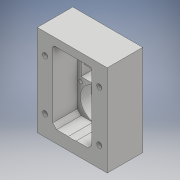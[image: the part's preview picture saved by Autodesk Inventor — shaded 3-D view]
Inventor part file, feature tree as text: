
AUTODESK INVENTOR PART (.ipt)
format: ipt  version: 2018 (Build 220112000, 112)  size: 443,904 bytes
history: native  units: mm
features: sketch x22, projected_geometry x19, extrude x18, hole x4, fillet x3, chamfer x1, mirror x1
ambient origin geometry x8: Origin, YZ Plane, XZ Plane, XY Plane, X Axis, Y Axis, Z Axis, Center Point
bodies: Solid1 (feature_tree)
feature tree (68):
  extrude  "Extrusion1"  Depth=45.0mm
  extrude  "Extrusion2"  Depth=1.95mm
  hole  "Hole1"  [1 undecoded]
  hole  "Hole2"  [1 undecoded]
  fillet  "Fillet1"  Radius=14.0mm
  extrude  "Extrusion3"  Depth=18.5mm
  extrude  "Extrusion4"  Depth=10.0mm
  extrude  "Extrusion5"  Depth=2.195mm
  extrude  "Extrusion6"  Depth=20.5mm
  hole  "Hole3"  [1 undecoded]
  extrude  "Extrusion7"  Depth=0.5mm
  extrude  "Extrusion8"  Depth=5.0mm TaperAngle=0.0deg
  extrude  "Extrusion9"  Depth=10.0mm
  extrude  "Extrusion10"  Depth=10.0mm
  extrude  "Extrusion11"  Depth=14.5mm
  extrude  "Extrusion12"  Depth=20.0mm
  extrude  "Extrusion13"  Depth=5.0mm
  extrude  "Extrusion14"  Depth=5.0mm
  extrude  "Extrusion15"  Depth=5.0mm
  extrude  "Extrusion16"  Depth=5.0mm
  extrude  "Extrusion17"  Depth=5.0mm
  chamfer  "Chamfer1"  Distance=1.0mm
  fillet  "Fillet7"  Radius=20.7mm
  fillet  "Fillet8"  Radius=32.0mm
  mirror  "Mirror1"
  extrude  "Extrusion18"  Depth=5.0mm TaperAngle=0.0deg
  hole  "Hole5"  [1 undecoded]
  sketch  "Sketch1"  dims[d0=24.5mm d1=45.0mm]
  sketch  "Sketch2"  dims[d2=1.95mm d3=0.0mm d4=2.25mm]
  projected_geometry  "Projected Loop1"
  sketch  "Sketch3"  dims[d5=20.0mm d6=2.25mm]
  projected_geometry  "Projected Loop2"
  sketch  "Sketch4"  dims[d7=5.25mm d8=5.25mm d9=14.0mm]
  projected_geometry  "Projected Loop3"
  sketch  "Sketch5"  dims[d10=5.25mm d11=18.5mm]
  projected_geometry  "Projected Loop4"
  sketch  "Sketch6"  dims[d12=10.0mm d13=0.0mm d14=20.5mm]
  projected_geometry  "Projected Loop5"
  sketch  "Sketch7"  dims[d15=2.0mm d16=2.195mm]
  projected_geometry  "Projected Loop6"
  sketch  "Sketch8"  dims[d17=2.0mm]
  projected_geometry  "Projected Loop7"
  sketch  "Sketch9"  dims[d18=2.4mm d19=6.0mm d20=4.4mm d21=2.0mm d22=90.0deg d23=8.0mm d24=20.594885mm d25=20.5mm]
  projected_geometry  "Projected Loop8"
  projected_geometry  "Projected Loop9"
  sketch  "Sketch10"  dims[d26=26.65mm d27=2.0mm]
  projected_geometry  "Projected Loop10"
  projected_geometry  "Projected Loop11"
  sketch  "Sketch11"  dims[d28=2.0mm]
  projected_geometry  "Projected Loop12"
  sketch  "Sketch12"  dims[d29=2.4mm d30=6.0mm d31=4.4mm d32=2.0mm d33=90.0deg d34=8.0mm d35=20.594885mm d36=0.5mm]
  sketch  "Sketch13"  dims[d37=18.0mm d38=5.0mm d39=0.0mm]
  sketch  "Sketch14"  dims[d41=10.0mm d42=0.0mm d43=24.5mm]
  projected_geometry  "Projected Loop13"
  sketch  "Sketch15"  dims[d44=1.15mm d45=0.0mm d46=10.0mm]
  sketch  "Sketch16"  dims[d47=21.0mm d48=14.5mm]
  projected_geometry  "Projected Loop14"
  sketch  "Sketch17"  dims[d49=20.0mm d50=14.5mm]
  projected_geometry  "Projected Loop15"
  sketch  "Sketch18"  dims[d51=24.5mm d52=5.0mm]
  projected_geometry  "Projected Loop16"
  sketch  "Sketch19"  dims[d53=5.0mm d54=2.25mm]
  projected_geometry  "Projected Loop17"
  sketch  "Sketch20"  dims[d55=2.25mm d56=5.0mm]
  projected_geometry  "Projected Loop18"
  sketch  "Sketch22"  dims[d57=5.0mm d58=9.0mm]
  sketch  "Sketch24"  dims[d59=14.75mm d60=4.0mm d61=1.0mm d62=0.0mm d63=20.7mm d64=2.4mm d65=6.0mm d66=4.4mm d67=2.0mm d68=90.0deg d69=8.0mm d70=20.594885mm d72=32.0mm d73=5.0mm d74=0.0mm d75=1.0mm d76=0.0mm d77=12.25mm d78=0.0mm d80=8.0mm d81=4.5mm d82=0.0mm d84=0.2mm d85=0.0mm d86=21.0mm d87=0.5mm d88=0.0mm d91=8.0mm d92=0.0mm d93=5.0mm d94=0.0mm d95=5.0mm d96=0.0mm d98=0.2mm d99=0.0mm d100=0.2mm d101=0.0mm d102=2.5mm d103=2.0mm d104=45.0deg d105=1.5mm d114=0.5mm d115=22.55mm d116=0.0mm d117=5.0mm d118=5.0mm d119=13.0mm d120=13.0mm d121=3.2mm d122=6.0mm d123=6.3mm d124=2.0mm d125=90.0deg d126=8.0mm d127=20.594885mm]
  projected_geometry  "Projected Loop21"
note: 4 required parameter values undecoded (feature->parameter linkage not recoverable at this tier; creation-order binding heuristic only, values carry confidence <= 0.55)
